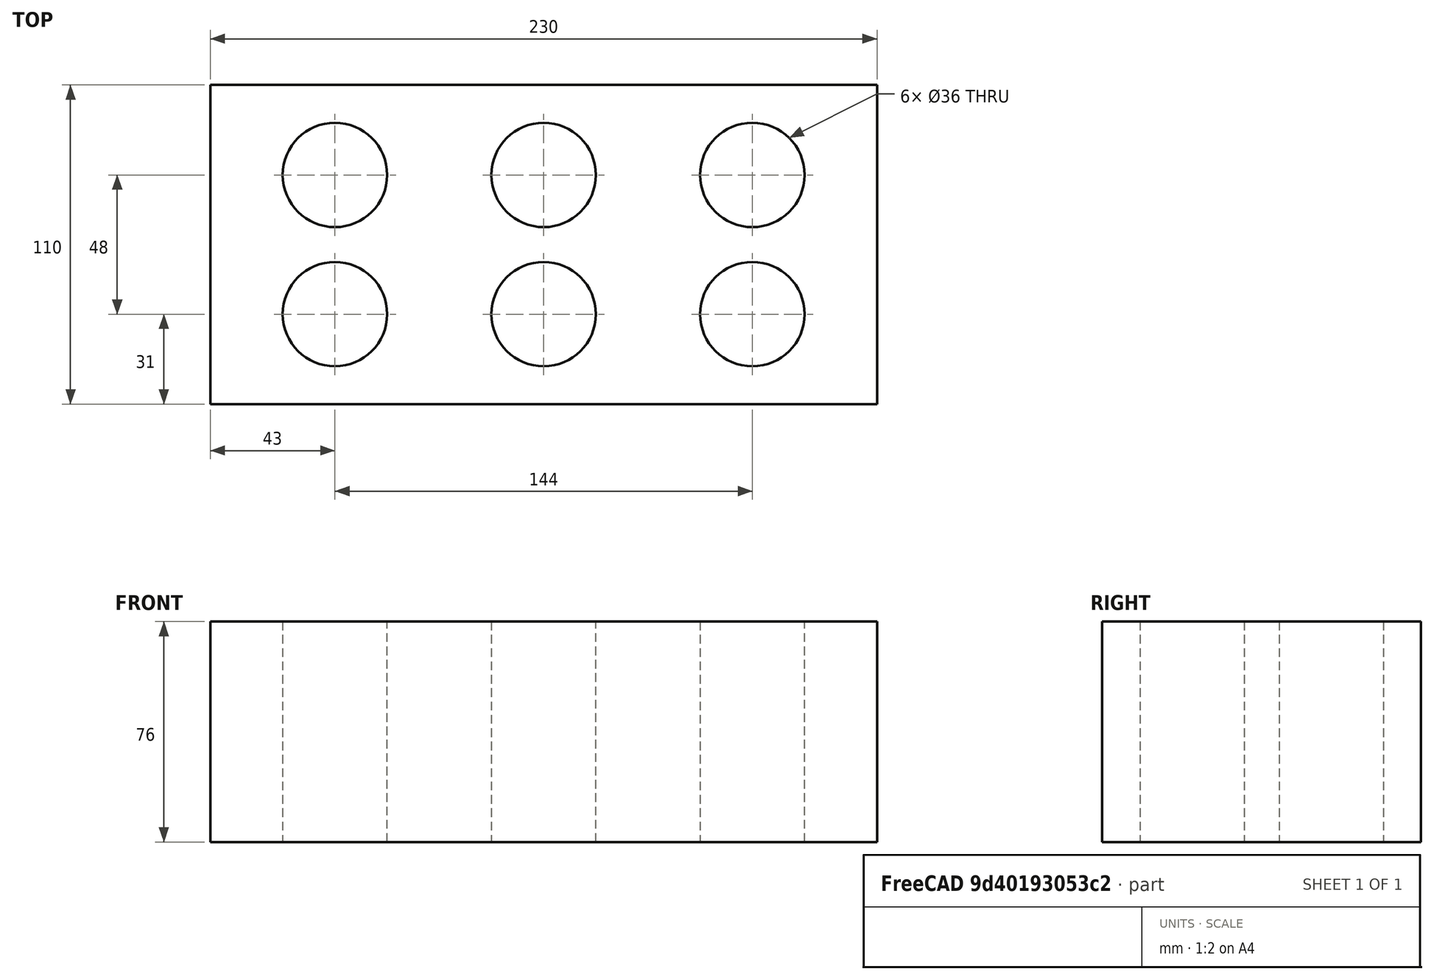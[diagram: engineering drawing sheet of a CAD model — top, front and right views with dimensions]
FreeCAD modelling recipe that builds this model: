
FCSTD DOCUMENT  (FreeCAD 0.20R29603 (Git))
Label: OJT1_T04R06_ladrillo
License: All rights reserved
LicenseURL: http://en.wikipedia.org/wiki/All_rights_reserved
objects: Part::Cylinder×6, Part::Cut×6, Part::Box×1
note: 13 computed .brp shape members not serialized (recipe doc carries the construction recipe); baked Part::Feature solids carry a one-line shape summary decoded from their .brp

FEATURE [Part::Box] Box  label="Cub"
  AttacherType = Attacher::AttachEngine3D
  Height = 76
  Length = 230
  Width = 110
FEATURE [Part::Cylinder] Cylinder  label="Cilindre"
  Angle = 360
  AttacherType = Attacher::AttachEngine3D
  FirstAngle = 0
  Height = 76
  Placement = pos=(43,79,0) rot=(0,0,1;0rad)
  Radius = 18
  SecondAngle = 0
FEATURE [Part::Cylinder] Cylinder001  label="Cilindre001"
  Angle = 360
  AttacherType = Attacher::AttachEngine3D
  FirstAngle = 0
  Height = 76
  Placement = pos=(43,31,0) rot=(0,0,1;0rad)
  Radius = 18
  SecondAngle = 0
FEATURE [Part::Cylinder] Cylinder002  label="Cilindre002"
  Angle = 360
  AttacherType = Attacher::AttachEngine3D
  FirstAngle = 0
  Height = 76
  Placement = pos=(115,79,0) rot=(0,0,1;0rad)
  Radius = 18
  SecondAngle = 0
FEATURE [Part::Cylinder] Cylinder003  label="Cilindre003"
  Angle = 360
  AttacherType = Attacher::AttachEngine3D
  FirstAngle = 0
  Height = 76
  Placement = pos=(115,31,0) rot=(0,0,1;0rad)
  Radius = 18
  SecondAngle = 0
FEATURE [Part::Cylinder] Cylinder004  label="Cilindre004"
  Angle = 360
  AttacherType = Attacher::AttachEngine3D
  FirstAngle = 0
  Height = 76
  Placement = pos=(187,31,0) rot=(0,0,1;0rad)
  Radius = 18
  SecondAngle = 0
FEATURE [Part::Cylinder] Cylinder005  label="Cilindre005"
  Angle = 360
  AttacherType = Attacher::AttachEngine3D
  FirstAngle = 0
  Height = 76
  Placement = pos=(187,79,0) rot=(0,0,1;0rad)
  Radius = 18
  SecondAngle = 0
FEATURE [Part::Cut] Cut
  Base = -> Box
  Tool = -> Cylinder
FEATURE [Part::Cut] Cut001
  Base = -> Cut
  Tool = -> Cylinder001
FEATURE [Part::Cut] Cut002
  Base = -> Cut001
  Tool = -> Cylinder002
FEATURE [Part::Cut] Cut003
  Base = -> Cut002
  Tool = -> Cylinder003
FEATURE [Part::Cut] Cut004
  Base = -> Cut003
  Tool = -> Cylinder004
FEATURE [Part::Cut] Cut005
  Base = -> Cut004
  Tool = -> Cylinder005
